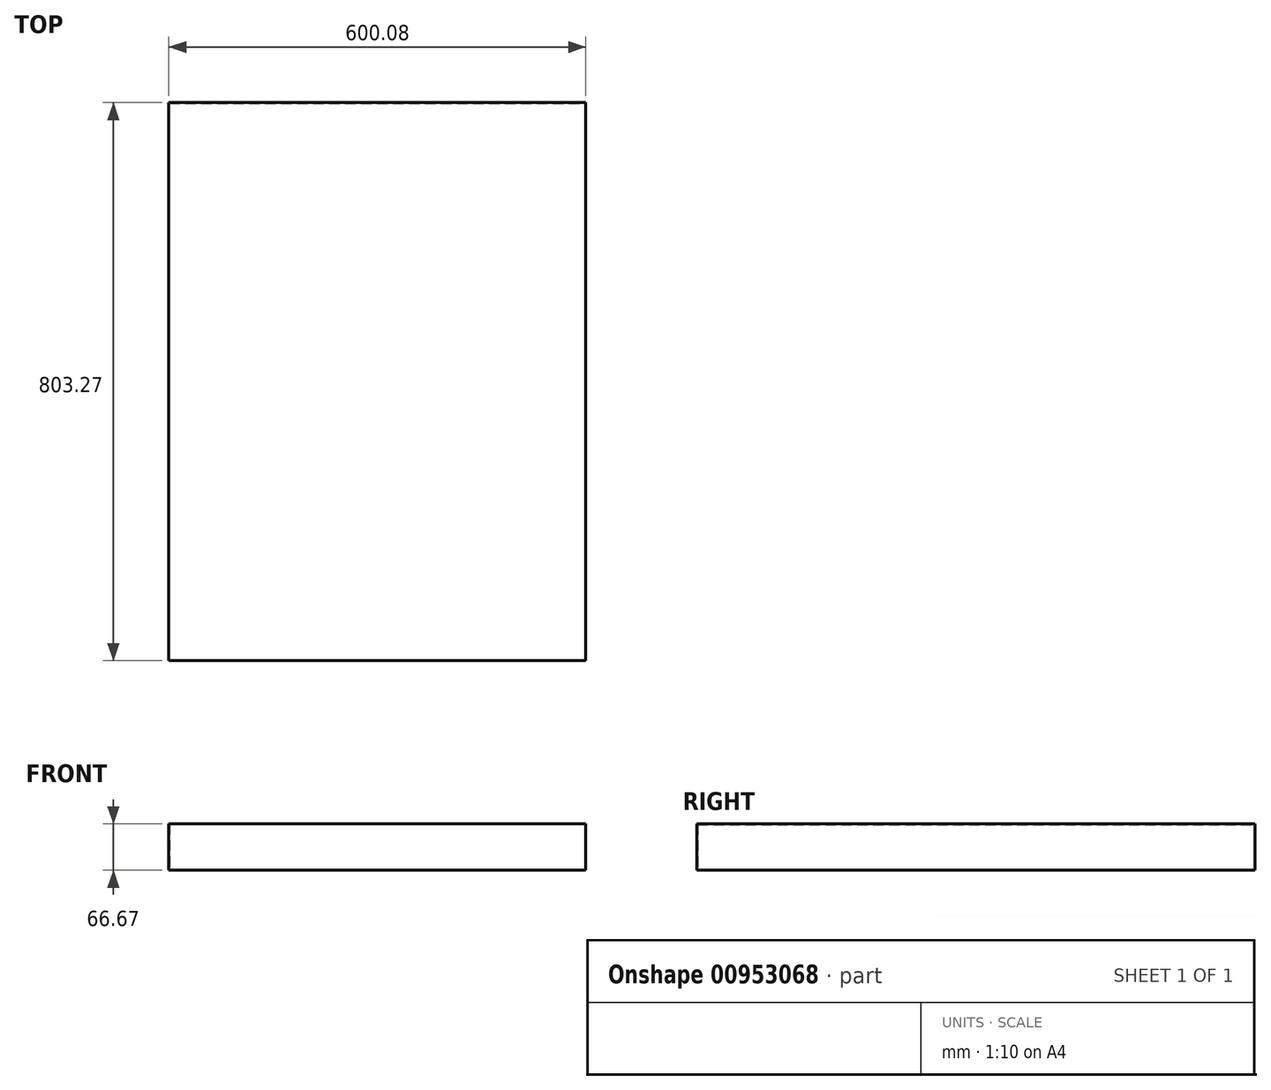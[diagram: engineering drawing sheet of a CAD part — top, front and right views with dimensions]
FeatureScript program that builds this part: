
annotation { "Feature Type Name" : "Feature", "Feature Type Description" : "" }
export const myFeature = defineFeature(function(context is Context, id is Id, definition is map)
    precondition{}
    {
        {
            var Q0;
            Q0=qCreatedBy(makeId("Top.planeOp"),FACE);
            var sketch = newSketch(context, id + "F0", { "sketchPlane" : qUnion([Q0])});
            skLineSegment(sketch, "E0", {"start": v(0, 0) * mm, "end": v(-600.08, 0) * mm});
            skLineSegment(sketch, "E1", {"start": v(-600.08, 0) * mm, "end": v(-600.08, 803.27) * mm});
            skLineSegment(sketch, "E2", {"start": v(-600.08, 803.27) * mm, "end": v(0, 803.27) * mm});
            skLineSegment(sketch, "E3", {"start": v(0, 803.27) * mm, "end": v(0, 0) * mm});
            skSolve(sketch);
        }
        {
            var Q0;
            Q0 = qSketchRegion(id + "F0", true);
            extrude(context, id + "F1", {"entities" : qUnion([Q0]), "depth" : 66.67 * mm, "offsetDistance" : 25.4 * mm});
        }
        {
            var Q0;
            Q0=makeQuery(id+"F1.opExtrude","CAP_FACE",FACE,{"disambiguationData":[OSD([sQuery(id+"F0.wireOp",EDGE,"E0"),sQuery(id+"F0.wireOp",EDGE,"E1"),sQuery(id+"F0.wireOp",EDGE,"E2"),sQuery(id+"F0.wireOp",EDGE,"E3")])],"isStart":true});
            var sketch = newSketch(context, id + "F2", { "sketchPlane" : qUnion([Q0])});
            skLineSegment(sketch, "E4", {"start": v(-599.26, -0.81) * mm, "end": v(-599.26, -802.46) * mm});
            skLineSegment(sketch, "E5", {"start": v(-599.26, -802.46) * mm, "end": v(-0.81, -802.46) * mm});
            skLineSegment(sketch, "E6", {"start": v(-0.81, -802.46) * mm, "end": v(-0.81, -0.81) * mm});
            skLineSegment(sketch, "E7", {"start": v(-0.81, -0.81) * mm, "end": v(-599.26, -0.81) * mm});
            skSolve(sketch);
        }
        {
            var Q0;
            Q0=makeQuery(id+"F2.imprint","IMPRINT",FACE,{"disambiguationData":[TD([[makeQuery(id+"F2.imprint","IMPRINT",EDGE,{"derivedFrom":sQuery(id+"F2.wireOp",EDGE,"E4")}),1.0]])]});
            extrude(context, id + "F3", {"entities" : qUnion([Q0]), "operationType" : NewBodyOperationType.REMOVE, "oppositeDirection" : true, "depth" : 65.86 * mm, "offsetDistance" : 25.4 * mm});
        }
    });
